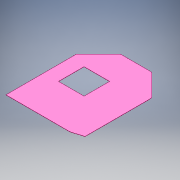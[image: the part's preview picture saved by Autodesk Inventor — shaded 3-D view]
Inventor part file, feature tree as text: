
AUTODESK INVENTOR PART (.ipt)
format: ipt  version: 2018 (Build 220112000, 112)  size: 142,848 bytes
history: native  units: mm
features: extrude x1, fillet x1, sketch x1
ambient origin geometry x8: Origin, YZ Plane, XZ Plane, XY Plane, X Axis, Y Axis, Z Axis, Center Point
bodies: Solid1 (feature_tree)
feature tree (3):
  extrude  "Extrusion1"  Depth=220.0mm
  fillet  "Fillet2"  Radius=220.0mm
  sketch  "Sketch1"  dims[d10=110.0mm d11=220.0mm d12=220.0mm d13=1.6mm d14=0.0mm d21=100.0mm d24=550.0mm d25=126.0mm d29=30.0mm d30=270.0mm d31=135.0deg d32=270.0mm d33=45.0deg d34=605.0mm d35=250.0mm d37=30.0mm]
